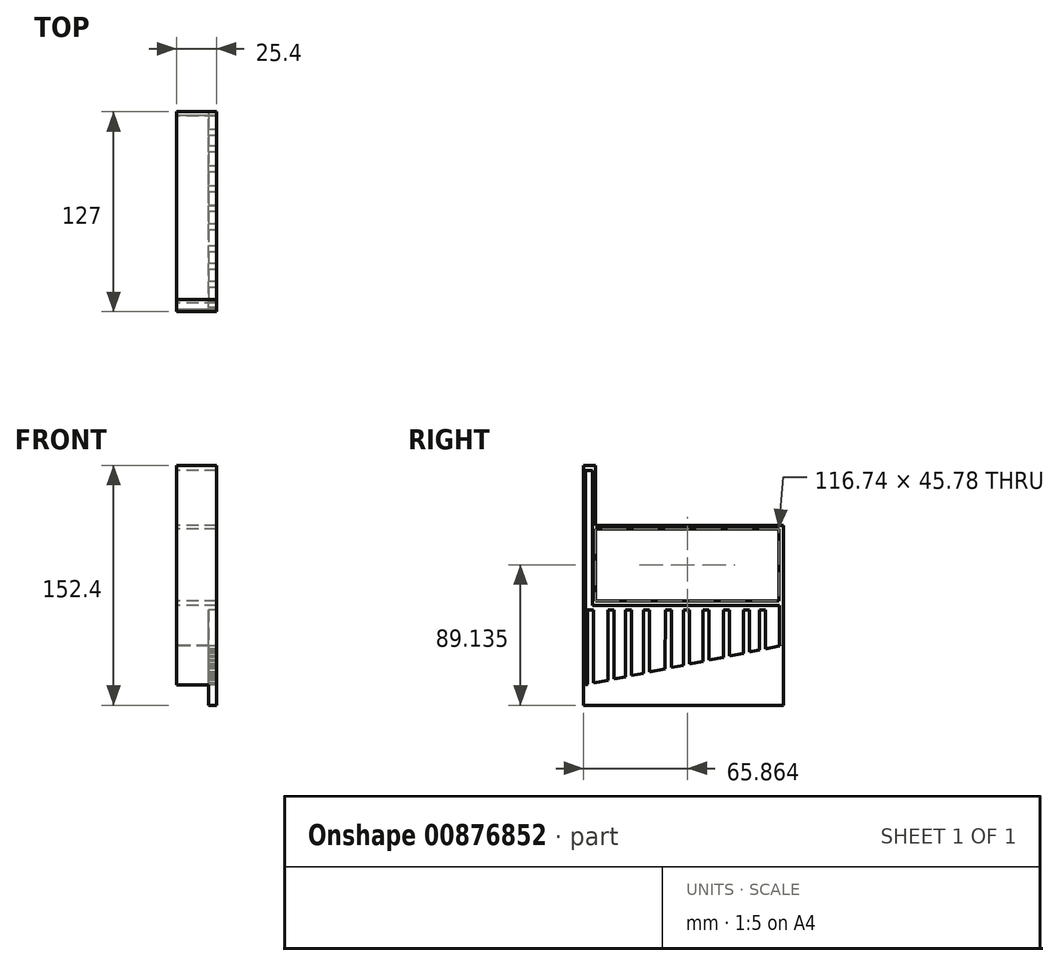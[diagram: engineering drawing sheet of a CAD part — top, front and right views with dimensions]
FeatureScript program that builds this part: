
annotation { "Feature Type Name" : "Feature", "Feature Type Description" : "" }
export const myFeature = defineFeature(function(context is Context, id is Id, definition is map)
    precondition{}
    {
        {
            var Q0;
            Q0=qCreatedBy(makeId("Right.planeOp"),FACE);
            var sketch = newSketch(context, id + "F0", { "sketchPlane" : qUnion([Q0])});
            skLineSegment(sketch, "E0.top", {"start": v(-60.93, -60.46) * mm, "end": v(66.07, -60.46) * mm});
            skLineSegment(sketch, "E0.left", {"start": v(-60.93, 91.94) * mm, "end": v(-60.93, -60.46) * mm});
            skLineSegment(sketch, "E1", {"start": v(-60.93, 91.94) * mm, "end": v(-53.3, 91.94) * mm});
            skLineSegment(sketch, "E2", {"start": v(66.07, 53.84) * mm, "end": v(-53.3, 53.84) * mm});
            skLineSegment(sketch, "E3", {"start": v(-53.3, 91.94) * mm, "end": v(-53.3, 53.84) * mm});
            skLineSegment(sketch, "E4", {"start": v(66.07, 53.84) * mm, "end": v(66.07, -60.46) * mm});
            skLineSegment(sketch, "E5", {"start": v(66.07, -60.46) * mm, "end": v(66.07, -22.36) * mm});
            skLineSegment(sketch, "E6", {"start": v(66.07, -22.36) * mm, "end": v(54.69, -24.64) * mm});
            skLineSegment(sketch, "E7", {"start": v(-60.93, 53.8) * mm, "end": v(-60.93, 3) * mm});
            skLineSegment(sketch, "E8", {"start": v(-60.93, 3) * mm, "end": v(66.07, 3) * mm});
            skLineSegment(sketch, "E9", {"start": v(66.07, -22.36) * mm, "end": v(66.07, -25.4) * mm});
            skLineSegment(sketch, "E10", {"start": v(66.07, -25.4) * mm, "end": v(66.07, -27.45) * mm});
            skLineSegment(sketch, "E11", {"start": v(66.07, -27.45) * mm, "end": v(66.07, -30.01) * mm});
            skLineSegment(sketch, "E12", {"start": v(66.07, -30.01) * mm, "end": v(66.07, -32.57) * mm});
            skLineSegment(sketch, "E13", {"start": v(66.07, -32.57) * mm, "end": v(66.07, -35.12) * mm});
            skLineSegment(sketch, "E14", {"start": v(66.07, -35.12) * mm, "end": v(66.07, -37.66) * mm});
            skLineSegment(sketch, "E15", {"start": v(66.07, -37.66) * mm, "end": v(66.07, -40.22) * mm});
            skLineSegment(sketch, "E16", {"start": v(66.07, -40.22) * mm, "end": v(66.07, -42.76) * mm});
            skLineSegment(sketch, "E17", {"start": v(66.07, -42.76) * mm, "end": v(66.07, -45.3) * mm});
            skLineSegment(sketch, "E18", {"start": v(50.88, -25.4) * mm, "end": v(50.88, 0) * mm});
            skLineSegment(sketch, "E19", {"start": v(50.88, 0) * mm, "end": v(54.69, 0) * mm});
            skLineSegment(sketch, "E20", {"start": v(54.69, 0) * mm, "end": v(54.69, -24.64) * mm});
            skLineSegment(sketch, "E21", {"start": v(40.64, -27.45) * mm, "end": v(40.64, 0) * mm});
            skLineSegment(sketch, "E22", {"start": v(40.64, 0) * mm, "end": v(44.46, 0) * mm});
            skLineSegment(sketch, "E23", {"start": v(44.46, 0) * mm, "end": v(44.46, -26.68) * mm});
            skLineSegment(sketch, "E24", {"start": v(27.81, -30.01) * mm, "end": v(27.81, 0) * mm});
            skLineSegment(sketch, "E25", {"start": v(27.81, 0) * mm, "end": v(31.62, 0) * mm});
            skLineSegment(sketch, "E26", {"start": v(31.62, 0) * mm, "end": v(31.62, -29.25) * mm});
            skLineSegment(sketch, "E27", {"start": v(15.02, -32.57) * mm, "end": v(15.02, 0) * mm});
            skLineSegment(sketch, "E28", {"start": v(15.02, 0) * mm, "end": v(18.83, 0) * mm});
            skLineSegment(sketch, "E29", {"start": v(18.83, 0) * mm, "end": v(18.83, -31.81) * mm});
            skLineSegment(sketch, "E30", {"start": v(2.57, -35.06) * mm, "end": v(2.57, 0) * mm});
            skLineSegment(sketch, "E31", {"start": v(2.57, 0) * mm, "end": v(6.38, 0) * mm});
            skLineSegment(sketch, "E32", {"start": v(6.38, 0) * mm, "end": v(6.35, -34.3) * mm});
            skLineSegment(sketch, "E33", {"start": v(-9.1, -37.4) * mm, "end": v(-8.98, 0) * mm});
            skLineSegment(sketch, "E34", {"start": v(-8.98, 0) * mm, "end": v(-5.17, 0) * mm});
            skLineSegment(sketch, "E35", {"start": v(-5.17, 0) * mm, "end": v(-5.17, -36.6) * mm});
            skLineSegment(sketch, "E36", {"start": v(-22.85, -40.15) * mm, "end": v(-22.85, 0) * mm});
            skLineSegment(sketch, "E37", {"start": v(-22.85, 0) * mm, "end": v(-19.04, -0.01) * mm});
            skLineSegment(sketch, "E38", {"start": v(-19.04, -0.01) * mm, "end": v(-19.04, -39.38) * mm});
            skLineSegment(sketch, "E39", {"start": v(-34.16, -42.4) * mm, "end": v(-34.16, 0) * mm});
            skLineSegment(sketch, "E40", {"start": v(-34.16, 0) * mm, "end": v(-30.35, 0) * mm});
            skLineSegment(sketch, "E41", {"start": v(-30.35, 0) * mm, "end": v(-30.35, -41.65) * mm});
            skLineSegment(sketch, "E42", {"start": v(-45.55, -44.68) * mm, "end": v(-45.55, 0) * mm});
            skLineSegment(sketch, "E43", {"start": v(-45.55, 0) * mm, "end": v(-41.74, -0.02) * mm});
            skLineSegment(sketch, "E44", {"start": v(-41.74, -0.02) * mm, "end": v(-41.74, -43.92) * mm});
            skLineSegment(sketch, "E45", {"start": v(-58.3, -47.23) * mm, "end": v(-58.3, 0) * mm});
            skLineSegment(sketch, "E46", {"start": v(-58.3, 0) * mm, "end": v(-54.48, 0) * mm});
            skLineSegment(sketch, "E47", {"start": v(-54.48, 0) * mm, "end": v(-54.48, -46.47) * mm});
            skLineSegment(sketch, "E48.bottom", {"start": v(63.3, 51.56) * mm, "end": v(-53.43, 51.56) * mm});
            skLineSegment(sketch, "E48.top", {"start": v(63.3, 5.79) * mm, "end": v(-53.43, 5.79) * mm});
            skLineSegment(sketch, "E48.left", {"start": v(63.3, 51.56) * mm, "end": v(63.3, 5.79) * mm});
            skLineSegment(sketch, "E48.right", {"start": v(-53.43, 51.56) * mm, "end": v(-53.43, 5.79) * mm});
            skLineSegment(sketch, "E49.trimOffspring", {"start": v(50.88, -25.4) * mm, "end": v(44.46, -26.68) * mm});
            skLineSegment(sketch, "E50.trimOffspring", {"start": v(40.64, -27.45) * mm, "end": v(31.62, -29.25) * mm});
            skLineSegment(sketch, "E51.trimOffspring", {"start": v(27.81, -30.01) * mm, "end": v(18.83, -31.81) * mm});
            skLineSegment(sketch, "E52.trimOffspring", {"start": v(15.02, -32.57) * mm, "end": v(6.35, -34.3) * mm});
            skLineSegment(sketch, "E53.trimOffspring", {"start": v(2.57, -35.06) * mm, "end": v(-5.17, -36.6) * mm});
            skLineSegment(sketch, "E54.trimOffspring", {"start": v(-9.1, -37.4) * mm, "end": v(-19.04, -39.38) * mm});
            skLineSegment(sketch, "E55.trimOffspring", {"start": v(-22.85, -40.15) * mm, "end": v(-30.35, -41.65) * mm});
            skLineSegment(sketch, "E56.trimOffspring", {"start": v(-34.16, -42.4) * mm, "end": v(-41.74, -43.92) * mm});
            skLineSegment(sketch, "E57.trimOffspring", {"start": v(-45.55, -44.68) * mm, "end": v(-54.48, -46.47) * mm});
            skLineSegment(sketch, "E58.trimOffspring", {"start": v(-58.3, -47.23) * mm, "end": v(-60.93, -47.76) * mm});
            skLineSegment(sketch, "E59", {"start": v(63.53, -22.87) * mm, "end": v(63.53, 3) * mm});
            skLineSegment(sketch, "E60", {"start": v(-59.6, -47.5) * mm, "end": v(-59.6, -16.74) * mm});
            skLineSegment(sketch, "E61", {"start": v(-59.6, -16.74) * mm, "end": v(-59.6, 3) * mm});
            skLineSegment(sketch, "E62", {"start": v(-59.6, 3) * mm, "end": v(-59.6, 88.46) * mm});
            skLineSegment(sketch, "E63", {"start": v(-59.6, 88.46) * mm, "end": v(-55.33, 88.46) * mm});
            skLineSegment(sketch, "E64", {"start": v(-55.33, 88.46) * mm, "end": v(-55.33, 54.32) * mm});
            skLineSegment(sketch, "E65", {"start": v(-55.33, 54.32) * mm, "end": v(-55.33, 3) * mm});
            skLineSegment(sketch, "E66", {"start": v(63.53, -22.87) * mm, "end": v(63.53, -56.74) * mm});
            skLineSegment(sketch, "E67", {"start": v(63.53, -56.74) * mm, "end": v(-58.6, -56.74) * mm});
            skLineSegment(sketch, "E68", {"start": v(-58.6, -56.74) * mm, "end": v(-58.6, -47.23) * mm});
            skSolve(sketch);
        }
        {
            var Q0;
            Q0 = qSketchRegion(id + "F0", true);
            var Q1;
            Q1=makeQuery(id+"F0.imprint","IMPRINT",FACE,{"disambiguationData":[TD([[makeQuery(id+"F0.imprint","IMPRINT",EDGE,{"derivedFrom":sQuery(id+"F0.wireOp",EDGE,"E18")}),-1.0]])]});
            extrude(context, id + "F1", {"entities" : qUnion([Q0, Q1]), "depth" : 25.4 * mm, "offsetDistance" : 25.4 * mm});
        }
        {
            var Q0;
            Q0=makeQuery(id+"F1.opExtrude","CAP_FACE",FACE,{"disambiguationData":[OSD([sQuery(id+"F0.wireOp",EDGE,"E0.top"),sQuery(id+"F0.wireOp",EDGE,"E0.left"),sQuery(id+"F0.wireOp",EDGE,"E1"),sQuery(id+"F0.wireOp",EDGE,"E2"),sQuery(id+"F0.wireOp",EDGE,"E3"),sQuery(id+"F0.wireOp",EDGE,"E4"),sQuery(id+"F0.wireOp",EDGE,"E5"),sQuery(id+"F0.wireOp",EDGE,"E6"),sQuery(id+"F0.wireOp",EDGE,"E7"),sQuery(id+"F0.wireOp",EDGE,"E8"),sQuery(id+"F0.wireOp",EDGE,"E9"),sQuery(id+"F0.wireOp",EDGE,"E10"),sQuery(id+"F0.wireOp",EDGE,"E11"),sQuery(id+"F0.wireOp",EDGE,"E12"),sQuery(id+"F0.wireOp",EDGE,"E13"),sQuery(id+"F0.wireOp",EDGE,"E14"),sQuery(id+"F0.wireOp",EDGE,"E15"),sQuery(id+"F0.wireOp",EDGE,"E16"),sQuery(id+"F0.wireOp",EDGE,"E17"),sQuery(id+"F0.wireOp",EDGE,"E18"),sQuery(id+"F0.wireOp",EDGE,"E19"),sQuery(id+"F0.wireOp",EDGE,"E20"),sQuery(id+"F0.wireOp",EDGE,"E21"),sQuery(id+"F0.wireOp",EDGE,"E22"),sQuery(id+"F0.wireOp",EDGE,"E23"),sQuery(id+"F0.wireOp",EDGE,"E24"),sQuery(id+"F0.wireOp",EDGE,"E25"),sQuery(id+"F0.wireOp",EDGE,"E26"),sQuery(id+"F0.wireOp",EDGE,"E27"),sQuery(id+"F0.wireOp",EDGE,"E28"),sQuery(id+"F0.wireOp",EDGE,"E29"),sQuery(id+"F0.wireOp",EDGE,"E30"),sQuery(id+"F0.wireOp",EDGE,"E31"),sQuery(id+"F0.wireOp",EDGE,"E32"),sQuery(id+"F0.wireOp",EDGE,"E33"),sQuery(id+"F0.wireOp",EDGE,"E34"),sQuery(id+"F0.wireOp",EDGE,"E35"),sQuery(id+"F0.wireOp",EDGE,"E36"),sQuery(id+"F0.wireOp",EDGE,"E37"),sQuery(id+"F0.wireOp",EDGE,"E38"),sQuery(id+"F0.wireOp",EDGE,"E39"),sQuery(id+"F0.wireOp",EDGE,"E40"),sQuery(id+"F0.wireOp",EDGE,"E41"),sQuery(id+"F0.wireOp",EDGE,"E42"),sQuery(id+"F0.wireOp",EDGE,"E43"),sQuery(id+"F0.wireOp",EDGE,"E44"),sQuery(id+"F0.wireOp",EDGE,"E45"),sQuery(id+"F0.wireOp",EDGE,"E46"),sQuery(id+"F0.wireOp",EDGE,"E47"),sQuery(id+"F0.wireOp",EDGE,"E48.bottom"),sQuery(id+"F0.wireOp",EDGE,"E48.top"),sQuery(id+"F0.wireOp",EDGE,"E48.left"),sQuery(id+"F0.wireOp",EDGE,"E48.right"),sQuery(id+"F0.wireOp",EDGE,"E49.trimOffspring"),sQuery(id+"F0.wireOp",EDGE,"E50.trimOffspring"),sQuery(id+"F0.wireOp",EDGE,"E51.trimOffspring"),sQuery(id+"F0.wireOp",EDGE,"E52.trimOffspring"),sQuery(id+"F0.wireOp",EDGE,"E53.trimOffspring"),sQuery(id+"F0.wireOp",EDGE,"E54.trimOffspring"),sQuery(id+"F0.wireOp",EDGE,"E55.trimOffspring"),sQuery(id+"F0.wireOp",EDGE,"E56.trimOffspring"),sQuery(id+"F0.wireOp",EDGE,"E57.trimOffspring"),sQuery(id+"F0.wireOp",EDGE,"E58.trimOffspring"),sQuery(id+"F0.wireOp",EDGE,"E59"),sQuery(id+"F0.wireOp",EDGE,"E60"),sQuery(id+"F0.wireOp",EDGE,"E61"),sQuery(id+"F0.wireOp",EDGE,"E62"),sQuery(id+"F0.wireOp",EDGE,"E63"),sQuery(id+"F0.wireOp",EDGE,"E64"),sQuery(id+"F0.wireOp",EDGE,"E65")])],"isStart":true});
            var sketch = newSketch(context, id + "F2", { "sketchPlane" : qUnion([Q0])});
            skLineSegment(sketch, "E69", {"start": v(-66.07, -22.87) * mm, "end": v(-66.07, -60.46) * mm});
            skLineSegment(sketch, "E70", {"start": v(-66.07, -60.46) * mm, "end": v(60.93, -60.46) * mm});
            skLineSegment(sketch, "E71", {"start": v(-54.69, -24.64) * mm, "end": v(-66.07, -22.36) * mm});
            skLineSegment(sketch, "E72", {"start": v(-54.69, -24.64) * mm, "end": v(-54.69, 0) * mm});
            skLineSegment(sketch, "E73", {"start": v(-54.69, 0) * mm, "end": v(-50.88, 0) * mm});
            skLineSegment(sketch, "E74", {"start": v(-50.88, 0) * mm, "end": v(-50.88, -25.4) * mm});
            skLineSegment(sketch, "E75", {"start": v(-50.88, -25.4) * mm, "end": v(-44.46, -26.68) * mm});
            skLineSegment(sketch, "E76", {"start": v(-44.46, -26.68) * mm, "end": v(-44.46, 0) * mm});
            skLineSegment(sketch, "E77", {"start": v(-44.46, 0) * mm, "end": v(-40.64, 0) * mm});
            skLineSegment(sketch, "E78", {"start": v(-40.64, 0) * mm, "end": v(-40.64, -27.45) * mm});
            skLineSegment(sketch, "E79", {"start": v(-40.64, -27.45) * mm, "end": v(-31.62, -29.25) * mm});
            skLineSegment(sketch, "E80", {"start": v(-31.62, -29.25) * mm, "end": v(-31.62, 0) * mm});
            skLineSegment(sketch, "E81", {"start": v(-31.62, 0) * mm, "end": v(-27.81, 0) * mm});
            skLineSegment(sketch, "E82", {"start": v(-27.81, 0) * mm, "end": v(-27.81, -30.01) * mm});
            skLineSegment(sketch, "E83", {"start": v(-27.81, -30.01) * mm, "end": v(-18.83, -31.81) * mm});
            skLineSegment(sketch, "E84", {"start": v(-18.83, -31.81) * mm, "end": v(-18.83, 0) * mm});
            skLineSegment(sketch, "E85", {"start": v(-18.83, 0) * mm, "end": v(-15.02, 0) * mm});
            skLineSegment(sketch, "E86", {"start": v(-15.02, 0) * mm, "end": v(-15.02, -32.57) * mm});
            skLineSegment(sketch, "E87", {"start": v(-15.02, -32.57) * mm, "end": v(-6.35, -34.3) * mm});
            skLineSegment(sketch, "E88", {"start": v(-6.35, -34.3) * mm, "end": v(-6.38, 0) * mm});
            skLineSegment(sketch, "E89", {"start": v(-6.38, 0) * mm, "end": v(-2.57, 0) * mm});
            skLineSegment(sketch, "E90", {"start": v(-2.57, 0) * mm, "end": v(-2.57, -35.06) * mm});
            skLineSegment(sketch, "E91", {"start": v(-2.57, -35.06) * mm, "end": v(5.17, -36.6) * mm});
            skLineSegment(sketch, "E92", {"start": v(5.17, -36.6) * mm, "end": v(5.17, 0) * mm});
            skLineSegment(sketch, "E93", {"start": v(5.17, 0) * mm, "end": v(8.98, 0) * mm});
            skLineSegment(sketch, "E94", {"start": v(8.98, 0) * mm, "end": v(9.1, -37.4) * mm});
            skLineSegment(sketch, "E95", {"start": v(9.1, -37.4) * mm, "end": v(19.04, -39.38) * mm});
            skLineSegment(sketch, "E96", {"start": v(19.04, -39.38) * mm, "end": v(19.04, -0.01) * mm});
            skLineSegment(sketch, "E97", {"start": v(19.04, -0.01) * mm, "end": v(22.85, 0) * mm});
            skLineSegment(sketch, "E98", {"start": v(22.85, 0) * mm, "end": v(22.85, -40.15) * mm});
            skLineSegment(sketch, "E99", {"start": v(22.85, -40.15) * mm, "end": v(30.35, -41.65) * mm});
            skLineSegment(sketch, "E100", {"start": v(30.35, -41.65) * mm, "end": v(30.35, 0) * mm});
            skLineSegment(sketch, "E101", {"start": v(30.35, 0) * mm, "end": v(34.16, 0) * mm});
            skLineSegment(sketch, "E102", {"start": v(34.16, 0) * mm, "end": v(34.16, -42.4) * mm});
            skLineSegment(sketch, "E103", {"start": v(34.16, -42.4) * mm, "end": v(41.74, -43.92) * mm});
            skLineSegment(sketch, "E104", {"start": v(41.74, -43.92) * mm, "end": v(41.74, -0.02) * mm});
            skLineSegment(sketch, "E105", {"start": v(41.74, -0.02) * mm, "end": v(45.55, 0) * mm});
            skLineSegment(sketch, "E106", {"start": v(45.55, 0) * mm, "end": v(45.55, -44.68) * mm});
            skLineSegment(sketch, "E107", {"start": v(45.55, -44.68) * mm, "end": v(54.48, -46.47) * mm});
            skLineSegment(sketch, "E108", {"start": v(54.48, -46.47) * mm, "end": v(54.48, 0) * mm});
            skLineSegment(sketch, "E109", {"start": v(54.48, 0) * mm, "end": v(58.3, 0) * mm});
            skLineSegment(sketch, "E110", {"start": v(58.3, 0) * mm, "end": v(58.3, -47.23) * mm});
            skLineSegment(sketch, "E111", {"start": v(58.3, -47.23) * mm, "end": v(60.93, -47.5) * mm});
            skLineSegment(sketch, "E112", {"start": v(60.93, -47.5) * mm, "end": v(60.93, -60.46) * mm});
            skSolve(sketch);
        }
        {
            var Q0;
            Q0 = qSketchRegion(id + "F2", true);
            var Q1;
            {var subQ6=sQuery(id+"F2.wireOp",EDGE,"E69");Q1=makeQuery(id+"F2.imprint","IMPRINT",FACE,{"disambiguationData":[TD([[makeQuery(id+"F2.imprint","IMPRINT",EDGE,{"derivedFrom":subQ6}),1.0]])]});}
            extrude(context, id + "F3", {"entities" : qUnion([Q0, Q1]), "operationType" : NewBodyOperationType.REMOVE, "oppositeDirection" : true, "depth" : 20.32 * mm, "offsetDistance" : 25.4 * mm});
        }
    });
